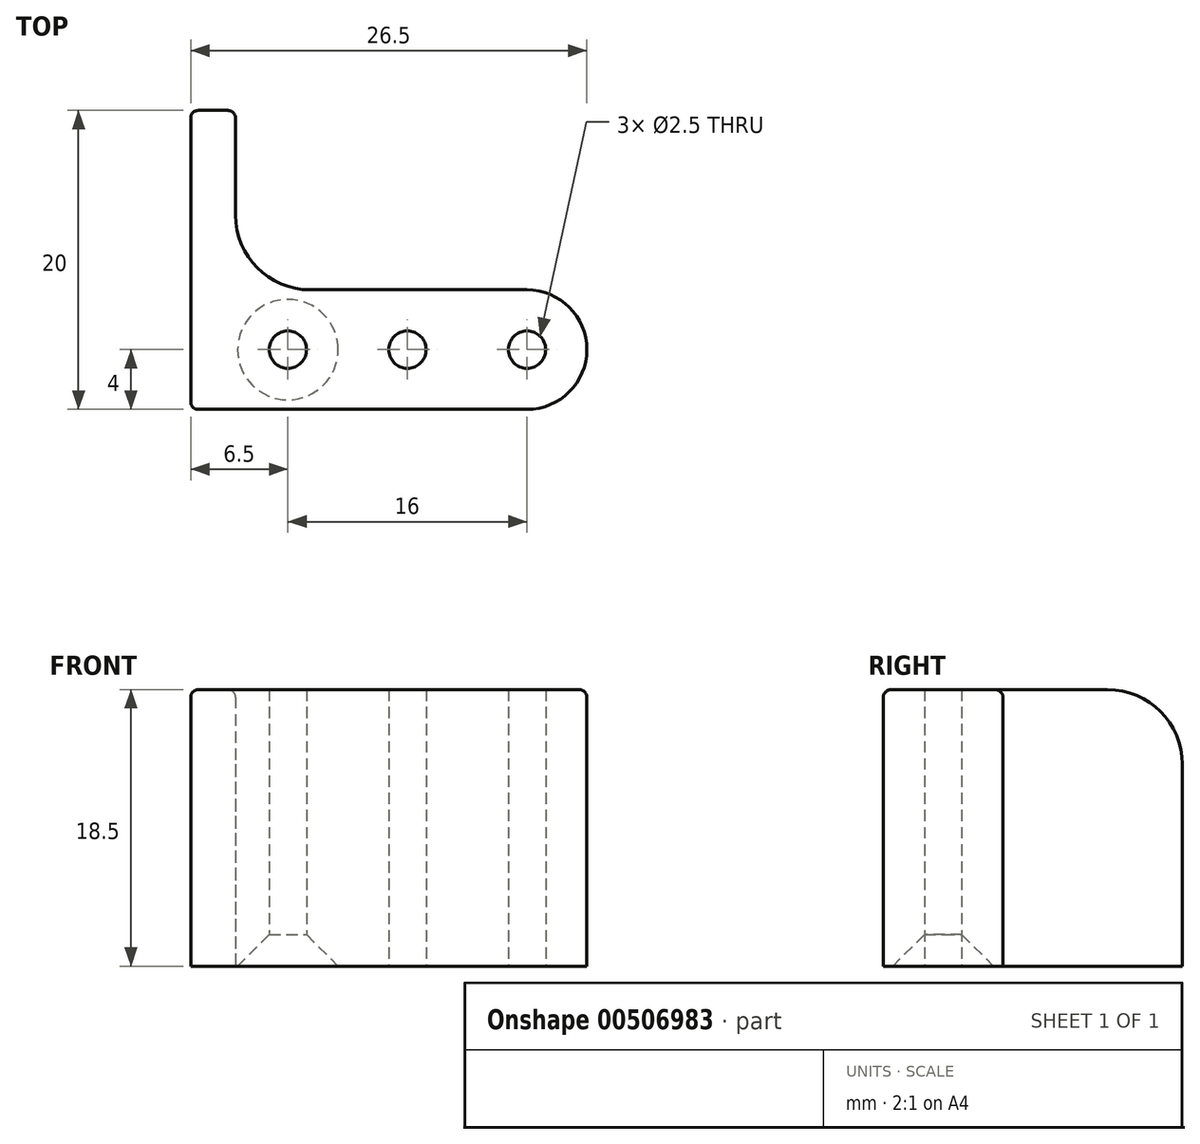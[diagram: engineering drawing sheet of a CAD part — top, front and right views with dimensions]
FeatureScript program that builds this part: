
annotation { "Feature Type Name" : "Feature", "Feature Type Description" : "" }
export const myFeature = defineFeature(function(context is Context, id is Id, definition is map)
    precondition{}
    {
        {
            var Q0;
            Q0=qCreatedBy(makeId("Top.planeOp"),FACE);
            var sketch = newSketch(context, id + "F0", { "sketchPlane" : qUnion([Q0])});
            skCircle(sketch, "E0", {"center": v(0, 0) * mm, "radius": 1.5 * mm});
            skCircle(sketch, "E1", {"center": v(8, 0) * mm, "radius": 1.5 * mm});
            skPoint(sketch, "E2", {"position": v(1.5, 0) * mm});
            skArc(sketch, "E3", {"start": v(8, -4) * mm, "mid": v(12, 0) * mm, "end": v(8, 4) * mm});
            skLineSegment(sketch, "E4.top", {"start": v(8, -4) * mm, "end": v(-14.5, -4) * mm});
            skLineSegment(sketch, "E5", {"start": v(-14.5, -4) * mm, "end": v(-14.5, 16) * mm});
            skLineSegment(sketch, "E6", {"start": v(-14.5, 16) * mm, "end": v(-11.5, 16) * mm});
            skLineSegment(sketch, "E7", {"start": v(8, 4) * mm, "end": v(-11.5, 4) * mm});
            skLineSegment(sketch, "E8", {"start": v(-11.5, 4) * mm, "end": v(-11.5, 16) * mm});
            skLineSegment(sketch, "E9", {"start": v(8, 0) * mm, "end": v(-11.5, 0) * mm, "construction": true});
            skCircle(sketch, "E10", {"center": v(-8, 0) * mm, "radius": 1.5 * mm});
            skSolve(sketch);
        }
        {
            var Q0;
            Q0=makeQuery(id+"F0.imprint","IMPRINT",FACE,{"disambiguationData":[TD([[makeQuery(id+"F0.imprint","IMPRINT",EDGE,{"derivedFrom":sQuery(id+"F0.wireOp",EDGE,"E0")}),-1.0]])]});
            var Q1;
            Q1=makeQuery(id+"F0.imprint","IMPRINT",FACE,{"disambiguationData":[TD([[makeQuery(id+"F0.imprint","IMPRINT",EDGE,{"derivedFrom":sQuery(id+"F0.wireOp",EDGE,"E0")}),1.0]])]});
            var Q2;
            Q2=makeQuery(id+"F0.imprint","IMPRINT",FACE,{"disambiguationData":[TD([[makeQuery(id+"F0.imprint","IMPRINT",EDGE,{"derivedFrom":sQuery(id+"F0.wireOp",EDGE,"E1")}),1.0]])]});
            var Q3;
            Q3=makeQuery(id+"F0.imprint","IMPRINT",FACE,{"disambiguationData":[TD([[makeQuery(id+"F0.imprint","IMPRINT",EDGE,{"derivedFrom":sQuery(id+"F0.wireOp",EDGE,"E10")}),1.0]])]});
            extrude(context, id + "F1", {"entities" : qUnion([Q0, Q1, Q2, Q3]), "depth" : 18.5 * mm, "offsetDistance" : 25 * mm});
        }
        {
            var Q0;
            Q0=sQuery(id+"F0.wireOp",VERTEX,"E1.center");
            var Q1;
            Q1=sQuery(id+"F0.wireOp",VERTEX,"E0.center");
            var Q2;
            Q2=makeQuery(id+"F1.opExtrude","SWEPT_BODY",BODY,{"disambiguationData":[OSD([sQuery(id+"F0.wireOp",EDGE,"QxN2yXpt-8XpC-Oixq-3axq-k1C0cWvr2tc3.bottom"),sQuery(id+"F0.wireOp",EDGE,"QxN2yXpt-8XpC-Oixq-3axq-k1C0cWvr2tc3.top"),sQuery(id+"F0.wireOp",EDGE,"QxN2yXpt-8XpC-Oixq-3axq-k1C0cWvr2tc3.left"),sQuery(id+"F0.wireOp",EDGE,"QxN2yXpt-8XpC-Oixq-3axq-k1C0cWvr2tc3.right"),sQuery(id+"F0.wireOp",EDGE,"E3"),sQuery(id+"F0.wireOp",EDGE,"E4.bottom"),sQuery(id+"F0.wireOp",EDGE,"E4.top"),sQuery(id+"F0.wireOp",EDGE,"d9ad3576-5a32-4b4a-8863-00f035f1b8a0.trimOffspring")])]});
            hole(context, id + "F2", {"style" : HoleStyle.SIMPLE, "endStyle" : HoleEndStyle.THROUGH, "oppositeDirection" : true, "standardTappedOrClearance" : lookupTablePath({ "standard" : "ISO", "engagement" : "75%", "pitch" : "0.5 mm", "size" : "M3", "type" : "Tapped" }), "standardBlindInLast" : lookupTablePath({ "standard" : "ISO", "fit" : "Normal", "engagement" : "75%", "pitch" : "0.5 mm", "size" : "M3", "type" : "Clearance & tapped" }), "holeDiameter" : 2.5 * mm, "majorDiameter" : 3 * mm, "showTappedDepth" : true, "isTappedThrough" : true, "tappedDepth" : 18.5 * mm, "tapClearance" : 3, "startFromSketch" : true, "locations" : qUnion([Q0, Q1]), "scope" : qUnion([Q2])});
        }
        {
            var Q0;
            Q0=sQuery(id+"F0.wireOp",VERTEX,"E10.center");
            var Q1;
            Q1=makeQuery(id+"F1.opExtrude","SWEPT_BODY",BODY,{"disambiguationData":[OSD([sQuery(id+"F0.wireOp",EDGE,"E3"),sQuery(id+"F0.wireOp",EDGE,"E4.top"),sQuery(id+"F0.wireOp",EDGE,"E5"),sQuery(id+"F0.wireOp",EDGE,"E6"),sQuery(id+"F0.wireOp",EDGE,"E7"),sQuery(id+"F0.wireOp",EDGE,"E8")])]});
            hole(context, id + "F3", {"style" : HoleStyle.C_SINK, "endStyle" : HoleEndStyle.THROUGH, "oppositeDirection" : true, "standardTappedOrClearance" : lookupTablePath({ "standard" : "ISO", "engagement" : "75%", "pitch" : "0.5 mm", "size" : "M3", "type" : "Tapped" }), "standardBlindInLast" : lookupTablePath({ "fit" : "Normal", "standard" : "ISO", "engagement" : "75%", "pitch" : "0.5 mm", "size" : "M3", "type" : "Clearance & tapped" }), "holeDiameter" : 2.5 * mm, "cSinkDiameter" : 6.72 * mm, "cSinkAngle" : 90 * degree, "majorDiameter" : 3 * mm, "showTappedDepth" : true, "isTappedThrough" : true, "tappedDepth" : 20 * mm, "tapClearance" : 3, "startFromSketch" : true, "locations" : qUnion([Q0]), "scope" : qUnion([Q1])});
        }
        {
            var Q0;
            Q0=makeQuery(id+"F1.opExtrude","SWEPT_EDGE",EDGE,{"disambiguationData":[OSD([sQuery(id+"F0.wireOp",EDGE,"E7"),sQuery(id+"F0.wireOp",EDGE,"E8")])]});
            var Q1;
            Q1=makeQuery(id+"F1.opExtrude","CAP_EDGE",EDGE,{"disambiguationData":[OSD([sQuery(id+"F0.wireOp",EDGE,"E6")])],"isStart":false});
            fillet(context, id + "F4", {"entities" : qUnion([Q0, Q1]), "tangentPropagation" : true, "radius" : 5 * mm, "defaultsChanged" : false, "vertexSettings" : [], "allowEdgeOverflow" : false});
        }
        {
            var Q0;
            Q0=makeQuery(id+"F1.opExtrude","CAP_EDGE",EDGE,{"disambiguationData":[OSD([sQuery(id+"F0.wireOp",EDGE,"E4.top")])],"isStart":false});
            var Q1;
            Q1=makeQuery(id+"F1.opExtrude","CAP_EDGE",EDGE,{"disambiguationData":[OSD([sQuery(id+"F0.wireOp",EDGE,"E5")])],"isStart":false});
            var Q2;
            Q2=makeQuery(id+"F1.opExtrude","CAP_EDGE",EDGE,{"disambiguationData":[OSD([sQuery(id+"F0.wireOp",EDGE,"E6")])],"isStart":false});
            var Q3;
            Q3=makeQuery(id+"F1.opExtrude","SWEPT_EDGE",EDGE,{"disambiguationData":[OSD([sQuery(id+"F0.wireOp",EDGE,"E4.top"),sQuery(id+"F0.wireOp",EDGE,"E5")])]});
            fillet(context, id + "F5", {"entities" : qUnion([Q0, Q1, Q2, Q3]), "tangentPropagation" : true, "radius" : 0.5 * mm, "defaultsChanged" : false, "vertexSettings" : [], "allowEdgeOverflow" : false});
        }
    });
